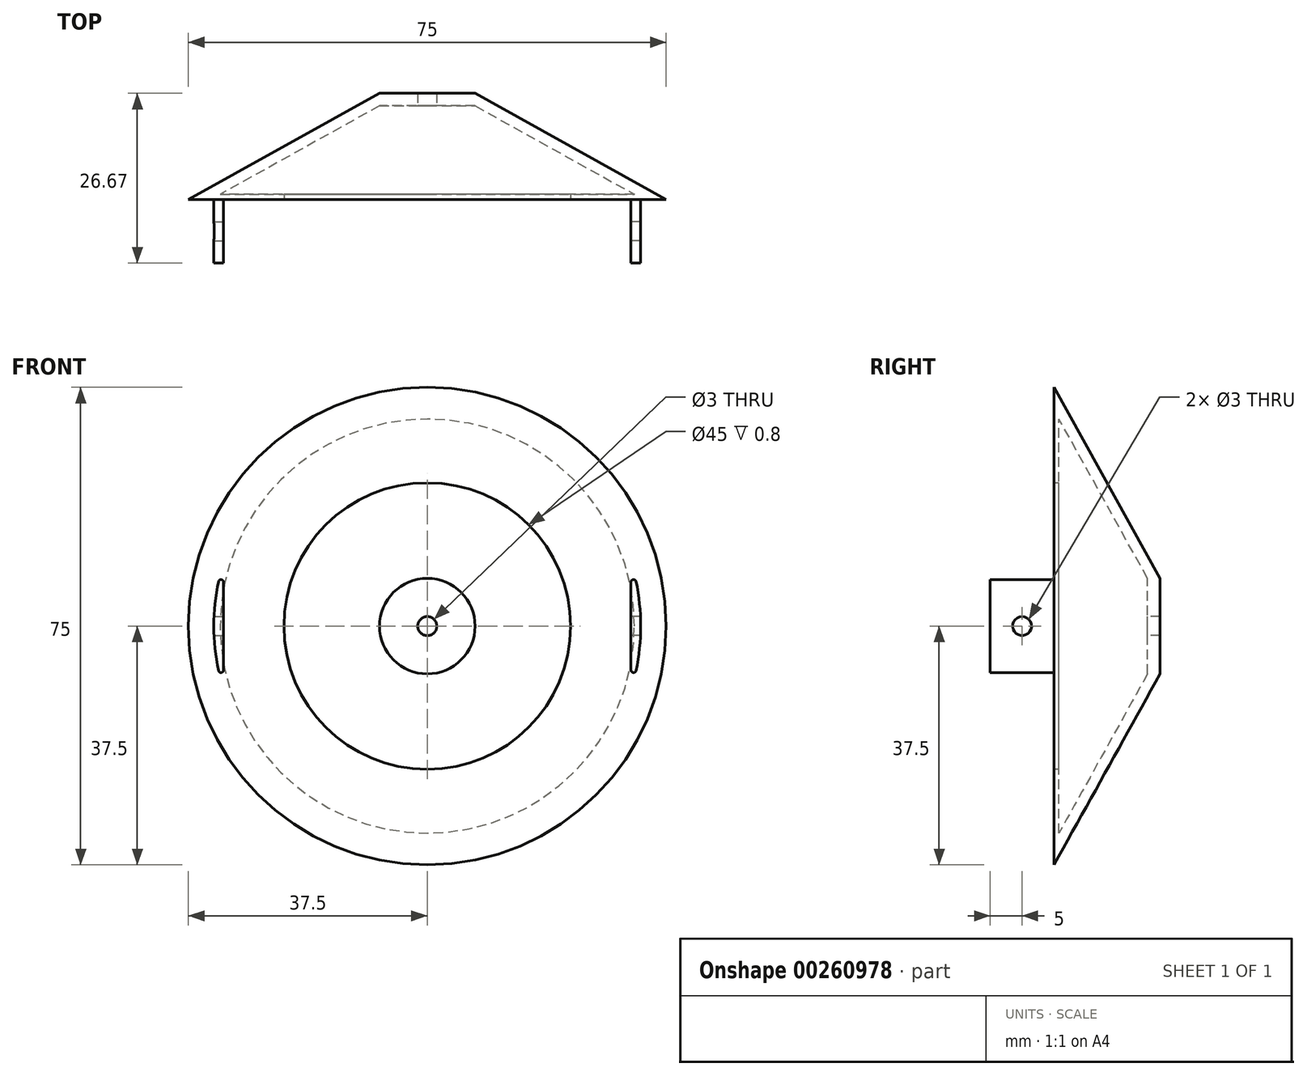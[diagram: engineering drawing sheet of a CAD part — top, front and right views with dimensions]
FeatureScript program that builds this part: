
annotation { "Feature Type Name" : "Feature", "Feature Type Description" : "" }
export const myFeature = defineFeature(function(context is Context, id is Id, definition is map)
    precondition{}
    {
        {
            var Q0;
            Q0=qCreatedBy(makeId("Top.planeOp"),FACE);
            var sketch = newSketch(context, id + "F0", { "sketchPlane" : qUnion([Q0])});
            skLineSegment(sketch, "E0", {"start": v(22.5, 0) * mm, "end": v(37.5, 0) * mm});
            skLineSegment(sketch, "E1", {"start": v(0, 0) * mm, "end": v(0, 0.4) * mm});
            skLineSegment(sketch, "E2", {"start": v(7.5, 16.67) * mm, "end": v(37.5, 0) * mm});
            skLineSegment(sketch, "E3", {"start": v(1.5, 16.67) * mm, "end": v(1.5, 14.69) * mm});
            skLineSegment(sketch, "E4", {"start": v(0, 0) * mm, "end": v(0, 20) * mm, "construction": true});
            skLineSegment(sketch, "E5", {"start": v(0, 20) * mm, "end": v(1.5, 20) * mm, "construction": true});
            skLineSegment(sketch, "E6", {"start": v(1.5, 16.67) * mm, "end": v(1.5, 14.69) * mm, "construction": true});
            skLineSegment(sketch, "E7", {"start": v(1.5, 14.69) * mm, "end": v(7.5, 14.69) * mm});
            skLineSegment(sketch, "E8", {"start": v(7.5, 14.69) * mm, "end": v(32.5, 0.8) * mm});
            skLineSegment(sketch, "E9", {"start": v(0, 0) * mm, "end": v(0, 0.8) * mm});
            skLineSegment(sketch, "E10", {"start": v(22.5, 0.8) * mm, "end": v(32.5, 0.8) * mm});
            skLineSegment(sketch, "E11", {"start": v(37.5, 0) * mm, "end": v(22.5, 0) * mm, "construction": true});
            skLineSegment(sketch, "E12", {"start": v(22.5, 0) * mm, "end": v(22.5, 0.8) * mm});
            skPoint(sketch, "E12.endSnap0", {"position": v(16.25, 0.8) * mm});
            skLineSegment(sketch, "E13", {"start": v(7.5, 14.69) * mm, "end": v(7.5, 16.67) * mm, "construction": true});
            skLineSegment(sketch, "E14", {"start": v(7.5, 16.67) * mm, "end": v(1.5, 16.67) * mm});
            skLineSegment(sketch, "E15", {"start": v(0, 0) * mm, "end": v(37.5, 0) * mm, "construction": true});
            skSolve(sketch);
        }
        {
            var Q0;
            Q0=makeQuery(id+"F0.imprint","IMPRINT",FACE,{"disambiguationData":[TD([[makeQuery(id+"F0.imprint","IMPRINT",EDGE,{"derivedFrom":sQuery(id+"F0.wireOp",EDGE,"WBFZH7eJ-8kSS-boB0-E7PE-2rGpITynkDhN")}),-1.0]])]});
            var Q1;
            Q1=makeQuery(id+"F0.imprint","IMPRINT",FACE,{"disambiguationData":[TD([[makeQuery(id+"F0.imprint","IMPRINT",EDGE,{"derivedFrom":sQuery(id+"F0.wireOp",EDGE,"E0")}),1.0]])]});
            var Q2;
            Q2=sQuery(id+"F0.wireOp",EDGE,"E4");
            revolve(context, id + "F1", {"entities" : qUnion([Q0, Q1]), "axis" : qUnion([Q2]), "revolveType" : RevolveType.FULL});
        }
        {
            var Q0;
            Q0=makeQuery(id+"F1.opRevolve","SWEPT_FACE",FACE,{"disambiguationData":[OSD([sQuery(id+"F0.wireOp",EDGE,"E0")])]});
            var sketch = newSketch(context, id + "F2", { "sketchPlane" : qUnion([Q0])});
            skArc(sketch, "E16", {"start": v(-31.97, 10) * mm, "mid": v(-33.5, 0) * mm, "end": v(-31.97, -10) * mm});
            skLineSegment(sketch, "E17", {"start": v(0, 0) * mm, "end": v(0, 10) * mm});
            skLineSegment(sketch, "E18", {"start": v(31.97, 10) * mm, "end": v(31.97, -10) * mm});
            skLineSegment(sketch, "E19", {"start": v(-31.97, -10) * mm, "end": v(-31.97, 10) * mm});
            skArc(sketch, "E20.trimOffspring", {"start": v(31.97, -10) * mm, "mid": v(33.5, 0) * mm, "end": v(31.97, 10) * mm});
            skSolve(sketch);
        }
        {
            var Q0;
            Q0=makeQuery(id+"F2.imprint","IMPRINT",FACE,{"disambiguationData":[TD([[makeQuery(id+"F2.imprint","IMPRINT",EDGE,{"derivedFrom":sQuery(id+"F2.wireOp",EDGE,"E16")}),1.0]])]});
            var Q1;
            Q1=makeQuery(id+"F2.imprint","IMPRINT",FACE,{"disambiguationData":[TD([[makeQuery(id+"F2.imprint","IMPRINT",EDGE,{"derivedFrom":sQuery(id+"F2.wireOp",EDGE,"E18")}),1.0]])]});
            extrude(context, id + "F3", {"entities" : qUnion([Q0, Q1]), "operationType" : NewBodyOperationType.ADD, "depth" : 10 * mm});
        }
        {
            var Q0;
            Q0=makeQuery(id+"F3.opExtrude","SWEPT_FACE",FACE,{"disambiguationData":[OSD([sQuery(id+"F2.wireOp",EDGE,"E19")])]});
            var sketch = newSketch(context, id + "F4", { "sketchPlane" : qUnion([Q0])});
            skLineSegment(sketch, "E21.0", {"start": v(-10, -10) * mm, "end": v(-10, 10) * mm, "construction": true});
            skLineSegment(sketch, "E22.0", {"start": v(0, -10) * mm, "end": v(0, 10) * mm, "construction": true});
            skLineSegment(sketch, "E23", {"start": v(-10, 0) * mm, "end": v(0, 0) * mm, "construction": true});
            skCircle(sketch, "E24", {"center": v(-5, 0) * mm, "radius": 1.5 * mm});
            skSolve(sketch);
        }
        {
            var Q0;
            Q0=makeQuery(id+"F4.imprint","IMPRINT",FACE,{"disambiguationData":[TD([[makeQuery(id+"F4.imprint","IMPRINT",EDGE,{"derivedFrom":sQuery(id+"F4.wireOp",EDGE,"E24")}),1.0]])]});
            var Q1;
            Q1=sQuery(id+"F4.wireOp",EDGE,"E24");
            extrude(context, id + "F5", {"entities" : qUnion([Q0]), "operationType" : NewBodyOperationType.REMOVE, "surfaceEntities" : qUnion([Q1]), "oppositeDirection" : true, "depth" : 25 * mm});
        }
        {
            var Q0;
            Q0=makeQuery(id+"F3.opExtrude","SWEPT_FACE",FACE,{"disambiguationData":[OSD([sQuery(id+"F2.wireOp",EDGE,"E18")])]});
            var sketch = newSketch(context, id + "F6", { "sketchPlane" : qUnion([Q0])});
            skLineSegment(sketch, "E25.0", {"start": v(10, 10) * mm, "end": v(10, -10) * mm, "construction": true});
            skLineSegment(sketch, "E26.0", {"start": v(0, 10) * mm, "end": v(0, -10) * mm, "construction": true});
            skLineSegment(sketch, "E27", {"start": v(0, 0) * mm, "end": v(10, 0) * mm, "construction": true});
            skCircle(sketch, "E28", {"center": v(5, 0) * mm, "radius": 1.5 * mm});
            skSolve(sketch);
        }
        {
            var Q0;
            Q0=makeQuery(id+"F6.imprint","IMPRINT",FACE,{"disambiguationData":[TD([[makeQuery(id+"F6.imprint","IMPRINT",EDGE,{"derivedFrom":sQuery(id+"F6.wireOp",EDGE,"E28")}),1.0]])]});
            var Q1;
            Q1=sQuery(id+"F6.wireOp",EDGE,"E28");
            extrude(context, id + "F7", {"entities" : qUnion([Q0]), "operationType" : NewBodyOperationType.REMOVE, "surfaceEntities" : qUnion([Q1]), "oppositeDirection" : true, "depth" : 25 * mm});
        }
        {
            var Q0;
            {var subQ0=sQuery(id+"F2.wireOp",EDGE,"E20.trimOffspring");var subQ1=sQuery(id+"F2.wireOp",EDGE,"E18");Q0=makeQuery(id+"F3.opExtrude","SWEPT_EDGE",EDGE,{"disambiguationData":[OSD([subQ1,subQ0]),TDD([makeQuery(id+"F2.imprint","INTERSECT",VERTEX,{"disambiguationData":[OD(1.0)],"derivedFrom":[subQ1,subQ0]})])]});}
            var Q1;
            {var subQ0=sQuery(id+"F2.wireOp",EDGE,"E20.trimOffspring");var subQ1=sQuery(id+"F2.wireOp",EDGE,"E18");Q1=makeQuery(id+"F3.opExtrude","SWEPT_EDGE",EDGE,{"disambiguationData":[OSD([subQ1,subQ0]),TDD([makeQuery(id+"F2.imprint","INTERSECT",VERTEX,{"disambiguationData":[OD(0.0)],"derivedFrom":[subQ1,subQ0]})])]});}
            var Q2;
            {var subQ0=sQuery(id+"F2.wireOp",EDGE,"E19");var subQ1=sQuery(id+"F2.wireOp",EDGE,"E16");Q2=makeQuery(id+"F3.opExtrude","SWEPT_EDGE",EDGE,{"disambiguationData":[OSD([subQ1,subQ0]),TDD([makeQuery(id+"F2.imprint","INTERSECT",VERTEX,{"disambiguationData":[OD(1.0)],"derivedFrom":[subQ1,subQ0]})])]});}
            var Q3;
            {var subQ0=sQuery(id+"F2.wireOp",EDGE,"E19");var subQ1=sQuery(id+"F2.wireOp",EDGE,"E16");Q3=makeQuery(id+"F3.opExtrude","SWEPT_EDGE",EDGE,{"disambiguationData":[OSD([subQ1,subQ0]),TDD([makeQuery(id+"F2.imprint","INTERSECT",VERTEX,{"disambiguationData":[OD(0.0)],"derivedFrom":[subQ1,subQ0]})])]});}
            fillet(context, id + "F8", {"entities" : qUnion([Q0, Q1, Q2, Q3]), "radius" : 0.4 * mm, "tangentPropagation" : true, "allowEdgeOverflow" : false});
        }
    });
